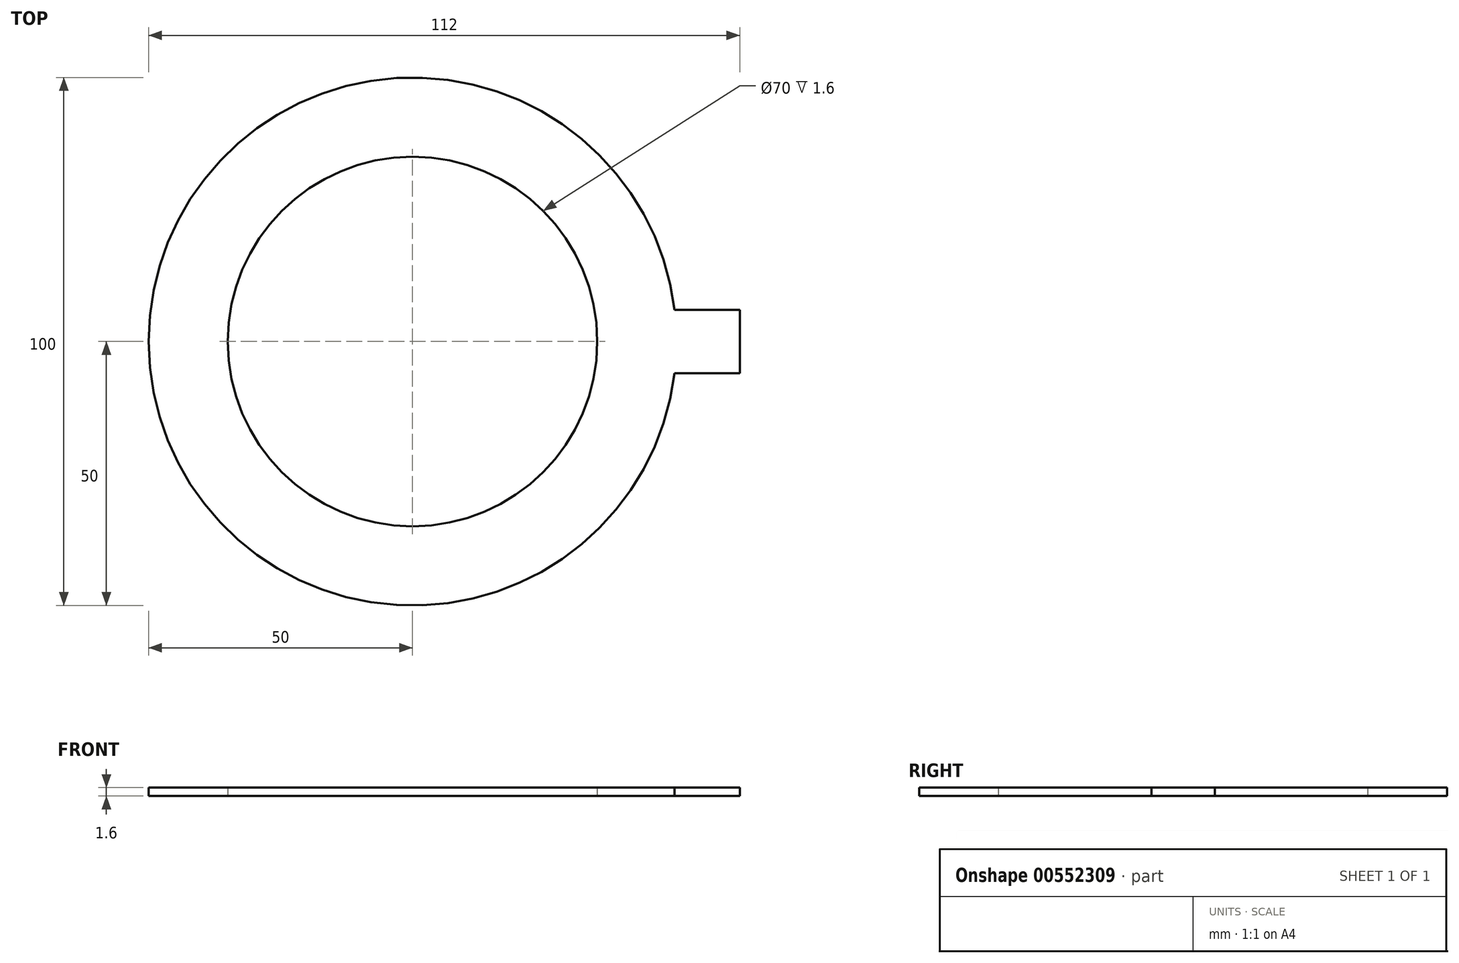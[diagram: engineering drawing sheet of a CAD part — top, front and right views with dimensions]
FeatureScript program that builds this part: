
annotation { "Feature Type Name" : "Feature", "Feature Type Description" : "" }
export const myFeature = defineFeature(function(context is Context, id is Id, definition is map)
    precondition{}
    {
        {
            var Q0;
            Q0=qCreatedBy(makeId("Top.planeOp"),FACE);
            var sketch = newSketch(context, id + "F0", { "sketchPlane" : qUnion([Q0])});
            skCircle(sketch, "E0", {"center": v(0, 0) * mm, "radius": 50 * mm});
            skCircle(sketch, "E1", {"center": v(0, 0) * mm, "radius": 35 * mm});
            skLineSegment(sketch, "E2.bottom", {"start": v(62, 6) * mm, "end": v(38, 6) * mm});
            skLineSegment(sketch, "E2.top", {"start": v(62, -6) * mm, "end": v(38, -6) * mm});
            skLineSegment(sketch, "E2.left", {"start": v(62, 6) * mm, "end": v(62, -6) * mm});
            skLineSegment(sketch, "E2.right", {"start": v(38, 6) * mm, "end": v(38, -6) * mm});
            skPoint(sketch, "E2.middle", {"position": v(50, 0) * mm});
            skLineSegment(sketch, "E3", {"start": v(0, 0) * mm, "end": v(-57.2, 57.2) * mm, "construction": true});
            skLineSegment(sketch, "E4", {"start": v(0, 0) * mm, "end": v(68.38, -68.38) * mm, "construction": true});
            skLineSegment(sketch, "E5", {"start": v(0, 0) * mm, "end": v(-53.17, -53.17) * mm, "construction": true});
            skLineSegment(sketch, "E6", {"start": v(0, 0) * mm, "end": v(54.34, 54.34) * mm, "construction": true});
            skLineSegment(sketch, "E7", {"start": v(-87.13, -16.42) * mm, "end": v(18.81, 89.52) * mm, "construction": true});
            skLineSegment(sketch, "E8", {"start": v(-83.05, 12.34) * mm, "end": v(15.43, -86.14) * mm, "construction": true});
            skLineSegment(sketch, "E9", {"start": v(99.07, 28.36) * mm, "end": v(-21.89, -92.6) * mm, "construction": true});
            skLineSegment(sketch, "E10", {"start": v(-8.91, 79.62) * mm, "end": v(94.27, -23.56) * mm, "construction": true});
            skSolve(sketch);
        }
        {
            var Q0;
            {var subQ0=sQuery(id+"F0.wireOp",EDGE,"E2.bottom");var subQ1=sQuery(id+"F0.wireOp",EDGE,"E0");var subQ2=makeQuery(id+"F0.imprint","INTERSECT",VERTEX,{"derivedFrom":[subQ1,subQ0]});Q0=makeQuery(id+"F0.imprint","IMPRINT",FACE,{"disambiguationData":[TD([[makeQuery(id+"F0.imprint","IMPRINT",EDGE,{"disambiguationData":[TD([[subQ2,-1.0]])],"derivedFrom":subQ1}),1.0]])]});}
            var Q1;
            {var subQ0=sQuery(id+"F0.wireOp",EDGE,"E2.bottom");var subQ1=sQuery(id+"F0.wireOp",EDGE,"E0");var subQ2=makeQuery(id+"F0.imprint","INTERSECT",VERTEX,{"derivedFrom":[subQ1,subQ0]});Q1=makeQuery(id+"F0.imprint","IMPRINT",FACE,{"disambiguationData":[TD([[makeQuery(id+"F0.imprint","IMPRINT",EDGE,{"disambiguationData":[TD([[subQ2,1.0]])],"derivedFrom":subQ1}),1.0]])]});}
            var Q2;
            {var subQ5=sQuery(id+"F0.wireOp",EDGE,"E2.left");Q2=makeQuery(id+"F0.imprint","IMPRINT",FACE,{"disambiguationData":[TD([[makeQuery(id+"F0.imprint","IMPRINT",EDGE,{"derivedFrom":subQ5}),-1.0]])]});}
            extrude(context, id + "F1", {"entities" : qUnion([Q0, Q1, Q2]), "depth" : 1.6 * mm, "offsetDistance" : 25 * mm});
        }
    });
